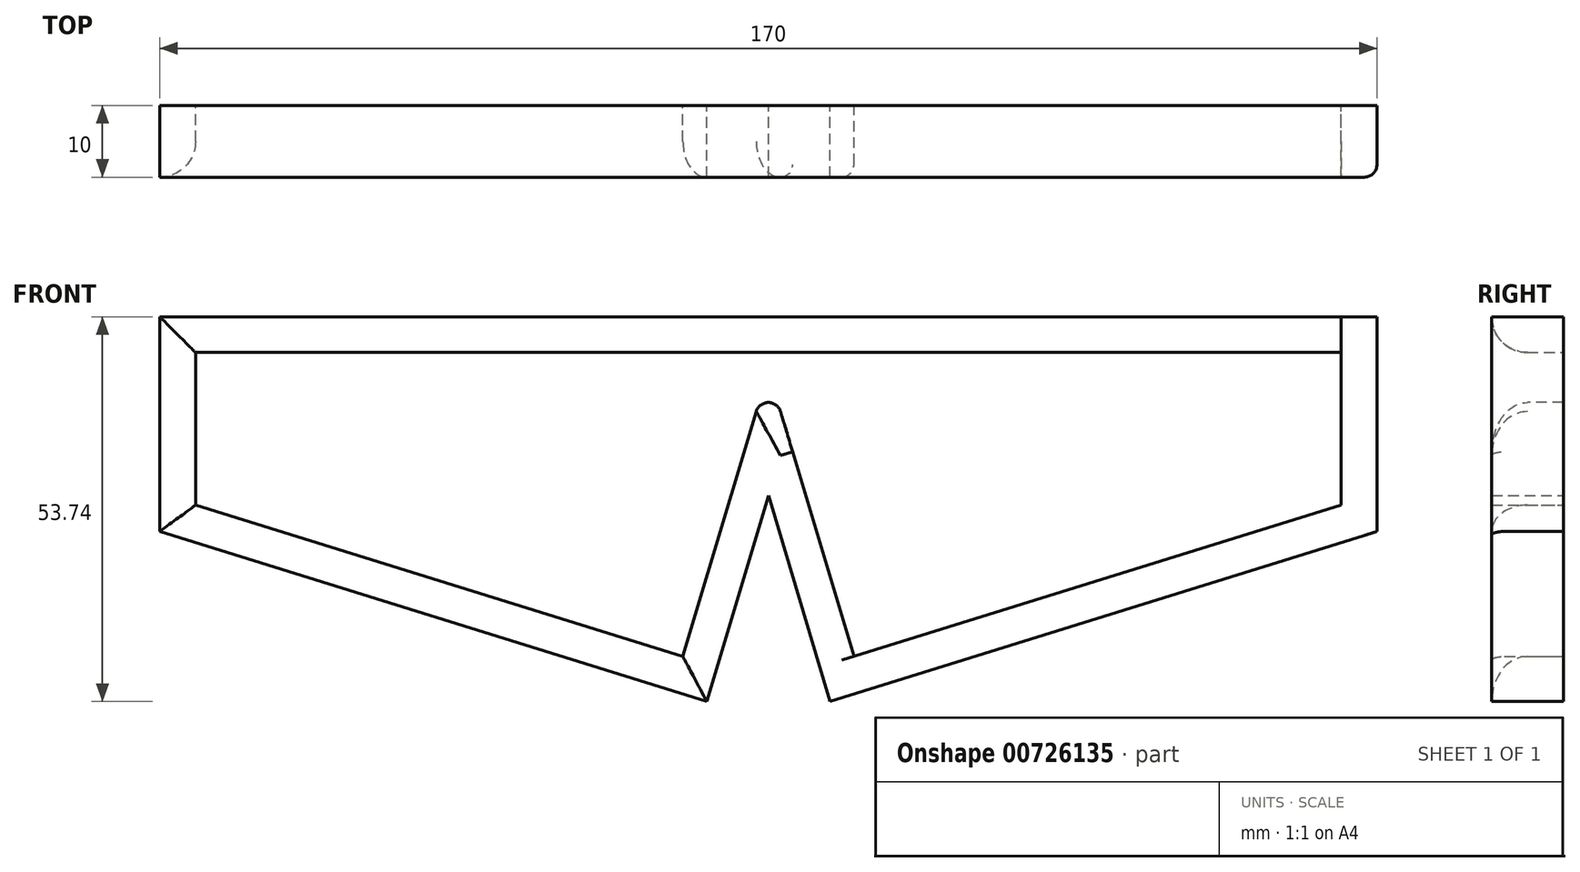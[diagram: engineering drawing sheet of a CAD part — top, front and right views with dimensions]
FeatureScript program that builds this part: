
annotation { "Feature Type Name" : "Feature", "Feature Type Description" : "" }
export const myFeature = defineFeature(function(context is Context, id is Id, definition is map)
    precondition{}
    {
        {
            var Q0;
            Q0=qCreatedBy(makeId("Front.planeOp"),FACE);
            var sketch = newSketch(context, id + "F0", { "sketchPlane" : qUnion([Q0])});
            skLineSegment(sketch, "E0.top", {"start": v(-12.38, 53.06) * mm, "end": v(-97.38, 53.06) * mm});
            skLineSegment(sketch, "E0.right", {"start": v(-97.38, 23.06) * mm, "end": v(-97.38, 53.06) * mm});
            skLineSegment(sketch, "E1", {"start": v(-20.99, -0.68) * mm, "end": v(-12.38, 28.06) * mm});
            skLineSegment(sketch, "E2", {"start": v(-20.99, -0.68) * mm, "end": v(-97.38, 23.06) * mm});
            skPoint(sketch, "E3.MirrorCS.end.orphan", {"position": v(-12.38, 53.06) * mm});
            skPoint(sketch, "E3.MirrorCS.start.orphan", {"position": v(-12.38, 78.06) * mm});
            skLineSegment(sketch, "E4.MirrorCS", {"start": v(72.62, 23.06) * mm, "end": v(72.62, 53.06) * mm});
            skLineSegment(sketch, "E5.MirrorCS", {"start": v(-3.78, -0.68) * mm, "end": v(72.62, 23.06) * mm});
            skLineSegment(sketch, "E6.MirrorCS", {"start": v(-3.78, -0.68) * mm, "end": v(-12.38, 28.06) * mm});
            skLineSegment(sketch, "E7.MirrorCS", {"start": v(-12.38, 53.06) * mm, "end": v(72.62, 53.06) * mm});
            skLineSegment(sketch, "E8.0", {"start": v(-12.38, 48.06) * mm, "end": v(67.62, 48.06) * mm});
            skLineSegment(sketch, "E8.1", {"start": v(67.62, 26.74) * mm, "end": v(67.62, 48.06) * mm});
            skLineSegment(sketch, "E8.2", {"start": v(-12.38, 48.06) * mm, "end": v(-92.38, 48.06) * mm});
            skLineSegment(sketch, "E8.3", {"start": v(-0.44, 5.6) * mm, "end": v(67.62, 26.74) * mm});
            skLineSegment(sketch, "E8.4", {"start": v(-92.38, 26.74) * mm, "end": v(-92.38, 48.06) * mm});
            skLineSegment(sketch, "E8.5", {"start": v(-24.33, 5.6) * mm, "end": v(-92.38, 26.74) * mm});
            skLineSegment(sketch, "E8.6", {"start": v(-24.33, 5.6) * mm, "end": v(-12.38, 45.5) * mm});
            skLineSegment(sketch, "E8.7", {"start": v(-0.44, 5.6) * mm, "end": v(-12.38, 45.5) * mm});
            skSolve(sketch);
        }
        {
            var Q0;
            Q0=makeQuery(id+"F0.imprint","IMPRINT",FACE,{"disambiguationData":[TD([[makeQuery(id+"F0.imprint","IMPRINT",EDGE,{"derivedFrom":sQuery(id+"F0.wireOp",EDGE,"E0.top")}),1.0]])]});
            extrude(context, id + "F1", {"entities" : qUnion([Q0]), "depth" : 10 * mm, "offsetDistance" : 25 * mm});
        }
        {
            var Q0;
            Q0=makeQuery(id+"F1.opExtrude","CAP_EDGE",EDGE,{"disambiguationData":[OSD([sQuery(id+"F0.wireOp",EDGE,"E8.0"),sQuery(id+"F0.wireOp",EDGE,"E8.2")])],"isStart":false});
            var Q1;
            Q1=makeQuery(id+"F1.opExtrude","CAP_EDGE",EDGE,{"disambiguationData":[OSD([sQuery(id+"F0.wireOp",EDGE,"E8.4")])],"isStart":false});
            var Q2;
            Q2=makeQuery(id+"F1.opExtrude","CAP_EDGE",EDGE,{"disambiguationData":[OSD([sQuery(id+"F0.wireOp",EDGE,"E8.5")])],"isStart":false});
            var Q3;
            Q3=makeQuery(id+"F1.opExtrude","CAP_EDGE",EDGE,{"disambiguationData":[OSD([sQuery(id+"F0.wireOp",EDGE,"E8.6")])],"isStart":false});
            fillet(context, id + "F2", {"entities" : qUnion([Q0, Q1, Q2, Q3]), "radius" : 5 * mm, "tangentPropagation" : true, "allowEdgeOverflow" : false});
        }
        {
            var Q0;
            Q0=makeQuery(id+"F1.opExtrude","CAP_EDGE",EDGE,{"disambiguationData":[OSD([sQuery(id+"F0.wireOp",EDGE,"E8.7")])],"isStart":false});
            var Q1;
            Q1=makeQuery(id+"F1.opExtrude","CAP_EDGE",EDGE,{"disambiguationData":[OSD([sQuery(id+"F0.wireOp",EDGE,"E4.MirrorCS")])],"isStart":false});
            var Q2;
            Q2=makeQuery(id+"F2.opFillet","BLEND_EDGE",EDGE,{"blendedFrom":[makeQuery(id+"F1.opExtrude","CAP_EDGE",EDGE,{"disambiguationData":[OSD([sQuery(id+"F0.wireOp",EDGE,"E8.6")])],"isStart":false}),makeQuery(id+"F1.opExtrude","SWEPT_FACE",FACE,{"disambiguationData":[OSD([sQuery(id+"F0.wireOp",EDGE,"E8.7")])]})],"blendedInto":[makeQuery(id+"F1.opExtrude","SWEPT_FACE",FACE,{"disambiguationData":[OSD([sQuery(id+"F0.wireOp",EDGE,"E8.7")])]})]});
            fillet(context, id + "F3", {"entities" : qUnion([Q0, Q1, Q2]), "radius" : 1.77 * mm, "tangentPropagation" : true, "allowEdgeOverflow" : false});
        }
    });
